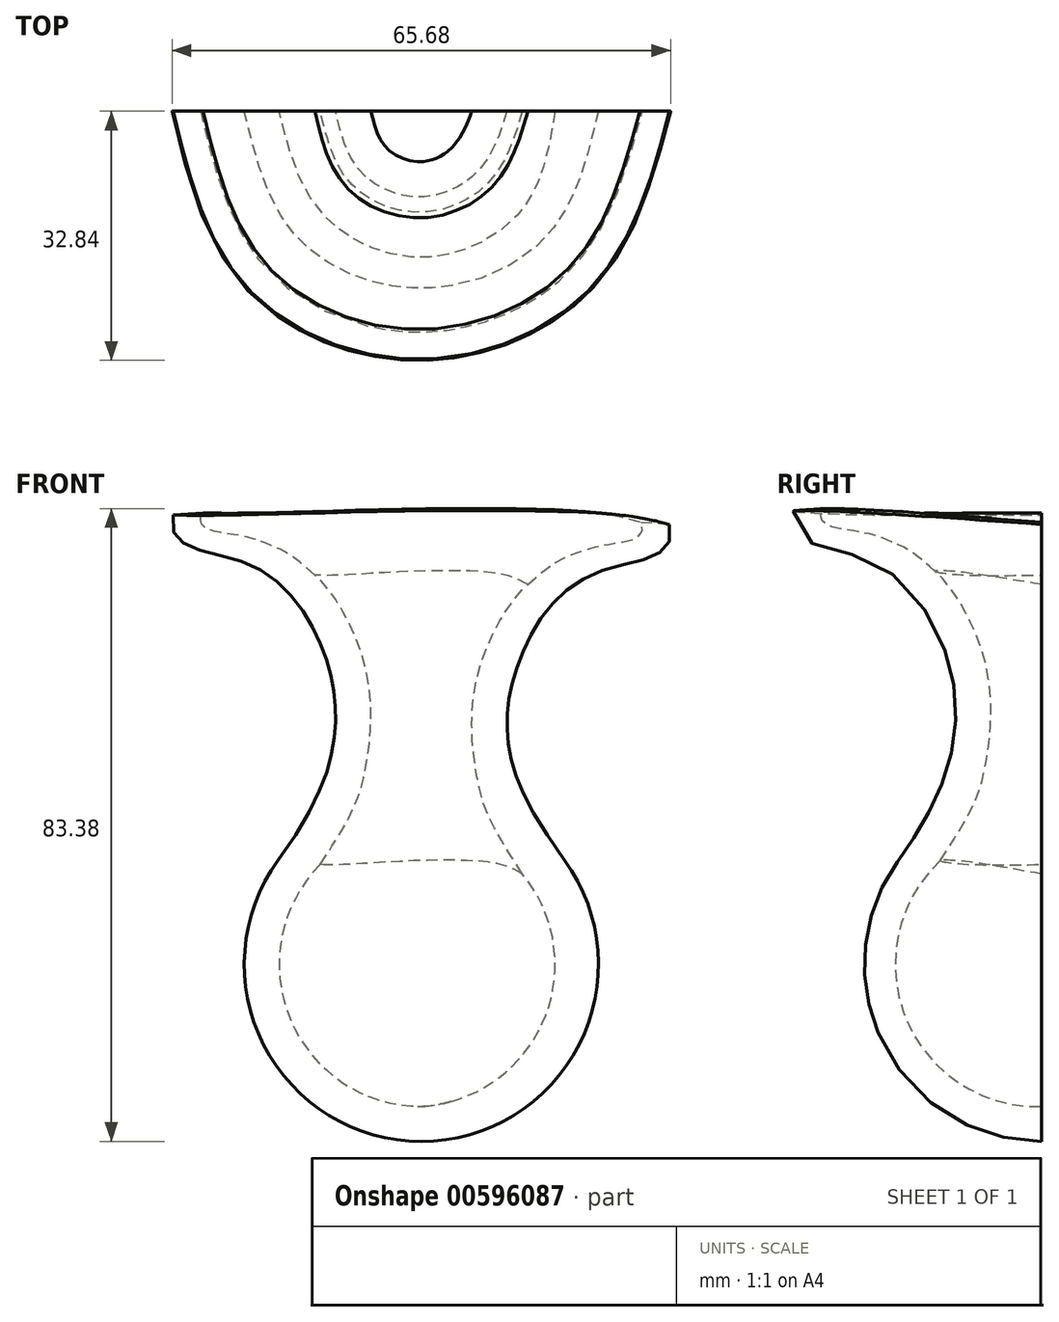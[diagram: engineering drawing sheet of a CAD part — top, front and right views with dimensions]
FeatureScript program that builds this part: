
annotation { "Feature Type Name" : "Feature", "Feature Type Description" : "" }
export const myFeature = defineFeature(function(context is Context, id is Id, definition is map)
    precondition{}
    {
        {
            var Q0;
            Q0=qCreatedBy(makeId("Front.planeOp"),FACE);
            var sketch = newSketch(context, id + "F0", { "sketchPlane" : qUnion([Q0])});
            skFitSpline(sketch, "E0", {"points": [v(-18.88, 13.69) * mm, v(-11.32, 31.6) * mm, v(-13.11, 41.8) * mm, v(-23.1, 52.87) * mm, v(-32.67, 59.2) * mm], "startDerivative": vector(59.38, 81.9) * mm, "endDerivative": vector(16.72, 63.85) * mm});
            skPoint(sketch, "E1.orphan", {"position": v(0, 59.2) * mm});
            skLineSegment(sketch, "E2.trimOffspring", {"start": v(0, -18.72) * mm, "end": v(0, -23.32) * mm});
            skFitSpline(sketch, "E3", {"points": [v(-13.32, 13.16) * mm, v(-7.45, 25.36) * mm, v(-7.45, 39.53) * mm, v(-14.04, 51.28) * mm], "startDerivative": vector(40, 60.94) * mm, "endDerivative": vector(-17.73, 13.1) * mm});
            skArc(sketch, "E4", {"start": v(-18.88, 13.69) * mm, "mid": v(-20.77, -10.6) * mm, "end": v(0, -23.32) * mm});
            skArc(sketch, "E5", {"start": v(-13.32, 13.16) * mm, "mid": v(-17.27, -7.22) * mm, "end": v(0, -18.72) * mm});
            skFitSpline(sketch, "E6", {"points": [v(-14.04, 51.28) * mm, v(-19.17, 54.93) * mm, v(-23.98, 56.49) * mm, v(-28.7, 57.72) * mm, v(-28.75, 59.48) * mm], "startDerivative": vector(-26.07, 24.13) * mm, "endDerivative": vector(8.86, 9.98) * mm});
            skLineSegment(sketch, "E7", {"start": v(-32.67, 59.2) * mm, "end": v(-28.75, 59.48) * mm});
            skSolve(sketch);
        }
        {
            var Q0;
            Q0=qCreatedBy(makeId("Front.planeOp"),FACE);
            var sketch = newSketch(context, id + "F1", { "sketchPlane" : qUnion([Q0])});
            skLineSegment(sketch, "E8", {"start": v(0, 0) * mm, "end": v(0, 58.67) * mm});
            skSolve(sketch);
        }
        {
            var Q0;
            Q0=sQuery(id+"F1.wireOp",EDGE,"E8");
            cPlane(context, id + "F2", {"entities" : qUnion([Q0]), "cplaneType" : CPlaneType.LINE_ANGLE, "offset" : 25.4 * mm, "angle" : 45 * degree, "width" : 152.4 * mm, "height" : 152.4 * mm});
        }
        {
            var Q0;
            Q0=qCreatedBy(id+"F2.planeOp",FACE);
            var sketch = newSketch(context, id + "F3", { "sketchPlane" : qUnion([Q0])});
            skFitSpline(sketch, "E9", {"points": [v(-18.88, 13.69) * mm, v(-10.9, 31.85) * mm, v(-12.7, 42.07) * mm, v(-22.69, 53.13) * mm, v(-32.25, 59.47) * mm], "startDerivative": vector(59.38, 81.9) * mm, "endDerivative": vector(16.72, 63.85) * mm});
            skLineSegment(sketch, "E10.trimOffspring", {"start": v(0, -18.72) * mm, "end": v(0, -23.32) * mm});
            skFitSpline(sketch, "E11", {"points": [v(-12.9, 13.42) * mm, v(-7.03, 25.62) * mm, v(-7.03, 39.8) * mm, v(-13.62, 51.55) * mm], "startDerivative": vector(40, 60.94) * mm, "endDerivative": vector(-17.73, 13.1) * mm});
            skArc(sketch, "E12", {"start": v(-18.88, 13.69) * mm, "mid": v(-20.77, -10.6) * mm, "end": v(0, -23.32) * mm});
            skArc(sketch, "E13", {"start": v(-12.9, 13.42) * mm, "mid": v(-17.22, -6.97) * mm, "end": v(0, -18.72) * mm});
            skFitSpline(sketch, "E14", {"points": [v(-13.62, 51.55) * mm, v(-18.74, 55.2) * mm, v(-23.55, 56.75) * mm, v(-28.27, 57.99) * mm, v(-28.33, 59.74) * mm], "startDerivative": vector(-26.07, 24.13) * mm, "endDerivative": vector(8.86, 9.98) * mm});
            skLineSegment(sketch, "E15", {"start": v(-32.25, 59.47) * mm, "end": v(-28.33, 59.74) * mm});
            skSolve(sketch);
        }
        {
            var Q0;
            Q0=sQuery(id+"F1.wireOp",EDGE,"E8");
            cPlane(context, id + "F4", {"entities" : qUnion([Q0]), "cplaneType" : CPlaneType.LINE_ANGLE, "offset" : 25.4 * mm, "angle" : 45 * degree, "oppositeDirection" : true, "width" : 152.4 * mm, "height" : 152.4 * mm});
        }
        {
            var Q0;
            Q0=qCreatedBy(id+"F4.planeOp",FACE);
            var sketch = newSketch(context, id + "F5", { "sketchPlane" : qUnion([Q0])});
            skFitSpline(sketch, "E16", {"points": [v(-18.88, 13.69) * mm, v(-11.32, 31.61) * mm, v(-13.11, 41.82) * mm, v(-23.1, 52.89) * mm, v(-32.67, 59.23) * mm], "startDerivative": vector(59.38, 81.9) * mm, "endDerivative": vector(16.72, 63.85) * mm});
            skLineSegment(sketch, "E17.trimOffspring", {"start": v(0, -18.72) * mm, "end": v(0, -23.32) * mm});
            skFitSpline(sketch, "E18", {"points": [v(-13.32, 13.17) * mm, v(-7.45, 25.38) * mm, v(-7.45, 39.55) * mm, v(-14.04, 51.3) * mm], "startDerivative": vector(40, 60.94) * mm, "endDerivative": vector(-17.73, 13.1) * mm});
            skArc(sketch, "E19", {"start": v(-18.88, 13.69) * mm, "mid": v(-20.77, -10.6) * mm, "end": v(0, -23.32) * mm});
            skArc(sketch, "E20", {"start": v(-13.32, 13.17) * mm, "mid": v(-17.3, -7.21) * mm, "end": v(0, -18.72) * mm});
            skFitSpline(sketch, "E21", {"points": [v(-14.04, 51.3) * mm, v(-19.17, 54.95) * mm, v(-23.98, 56.5) * mm, v(-28.7, 57.74) * mm, v(-28.75, 59.5) * mm], "startDerivative": vector(-26.07, 24.13) * mm, "endDerivative": vector(8.86, 9.98) * mm});
            skLineSegment(sketch, "E22", {"start": v(-32.67, 59.23) * mm, "end": v(-28.75, 59.5) * mm});
            skSolve(sketch);
        }
        {
            var Q0;
            Q0=sQuery(id+"F1.wireOp",EDGE,"E8");
            cPlane(context, id + "F6", {"entities" : qUnion([Q0]), "cplaneType" : CPlaneType.LINE_ANGLE, "offset" : 25.4 * mm, "angle" : 90 * degree, "width" : 152.4 * mm, "height" : 152.4 * mm});
        }
        {
            var Q0;
            Q0=qCreatedBy(id+"F6.planeOp",FACE);
            var sketch = newSketch(context, id + "F7", { "sketchPlane" : qUnion([Q0])});
            skFitSpline(sketch, "E23", {"points": [v(-18.88, 13.69) * mm, v(-11.32, 30.34) * mm, v(-13.11, 40.55) * mm, v(-23.1, 51.62) * mm, v(-32.67, 57.96) * mm], "startDerivative": vector(59.38, 81.9) * mm, "endDerivative": vector(16.72, 63.85) * mm});
            skLineSegment(sketch, "E24.trimOffspring", {"start": v(0, -18.72) * mm, "end": v(0, -23.32) * mm});
            skFitSpline(sketch, "E25", {"points": [v(-13.32, 11.9) * mm, v(-7.45, 24.1) * mm, v(-7.45, 38.28) * mm, v(-14.04, 50.03) * mm], "startDerivative": vector(40, 60.94) * mm, "endDerivative": vector(-17.73, 13.1) * mm});
            skArc(sketch, "E26", {"start": v(-18.88, 13.69) * mm, "mid": v(-20.77, -10.6) * mm, "end": v(0, -23.32) * mm});
            skArc(sketch, "E27", {"start": v(-13.32, 11.9) * mm, "mid": v(-16.06, -7.5) * mm, "end": v(0, -18.72) * mm});
            skFitSpline(sketch, "E28", {"points": [v(-14.04, 50.03) * mm, v(-19.17, 53.68) * mm, v(-23.98, 55.24) * mm, v(-28.7, 56.47) * mm, v(-28.75, 58.23) * mm], "startDerivative": vector(-26.07, 24.13) * mm, "endDerivative": vector(8.86, 9.98) * mm});
            skLineSegment(sketch, "E29", {"start": v(-32.67, 57.96) * mm, "end": v(-28.75, 58.23) * mm});
            skSolve(sketch);
        }
        {
            var Q0;
            Q0=sQuery(id+"F1.wireOp",EDGE,"E8");
            cPlane(context, id + "F8", {"entities" : qUnion([Q0]), "cplaneType" : CPlaneType.LINE_ANGLE, "offset" : 25.4 * mm, "angle" : 0 * degree, "width" : 152.4 * mm, "height" : 152.4 * mm});
        }
        {
            var Q0;
            Q0=qCreatedBy(id+"F8.planeOp",FACE);
            var sketch = newSketch(context, id + "F9", { "sketchPlane" : qUnion([Q0])});
            skFitSpline(sketch, "E30", {"points": [v(-18.88, 13.69) * mm, v(-11.32, 32.12) * mm, v(-13.11, 42.33) * mm, v(-23.1, 53.4) * mm, v(-32.67, 59.73) * mm], "startDerivative": vector(59.38, 81.9) * mm, "endDerivative": vector(16.72, 63.85) * mm});
            skLineSegment(sketch, "E31.trimOffspring", {"start": v(0, -18.72) * mm, "end": v(0, -23.32) * mm});
            skFitSpline(sketch, "E32", {"points": [v(-13.32, 13.68) * mm, v(-7.45, 25.89) * mm, v(-7.45, 40.06) * mm, v(-14.04, 51.81) * mm], "startDerivative": vector(40, 60.94) * mm, "endDerivative": vector(-17.73, 13.1) * mm});
            skArc(sketch, "E33", {"start": v(-18.88, 13.69) * mm, "mid": v(-20.77, -10.6) * mm, "end": v(0, -23.32) * mm});
            skArc(sketch, "E34", {"start": v(-13.32, 13.68) * mm, "mid": v(-17.86, -7.12) * mm, "end": v(0, -18.72) * mm});
            skFitSpline(sketch, "E35", {"points": [v(-14.04, 51.81) * mm, v(-19.17, 55.46) * mm, v(-23.98, 57.01) * mm, v(-28.7, 58.25) * mm, v(-28.75, 60) * mm], "startDerivative": vector(-26.07, 24.13) * mm, "endDerivative": vector(8.86, 9.98) * mm});
            skLineSegment(sketch, "E36", {"start": v(-32.67, 59.73) * mm, "end": v(-28.75, 60) * mm});
            skSolve(sketch);
        }
        {
            var Q0;
            Q0=makeQuery(id+"F7.imprint","IMPRINT",FACE,{"disambiguationData":[TD([[makeQuery(id+"F7.imprint","IMPRINT",EDGE,{"derivedFrom":sQuery(id+"F7.wireOp",EDGE,"E23")}),-1.0]])]});
            var Q1;
            Q1=makeQuery(id+"F3.imprint","IMPRINT",FACE,{"disambiguationData":[TD([[makeQuery(id+"F3.imprint","IMPRINT",EDGE,{"derivedFrom":sQuery(id+"F3.wireOp",EDGE,"E9")}),-1.0]])]});
            var Q2;
            Q2=makeQuery(id+"F9.imprint","IMPRINT",FACE,{"disambiguationData":[TD([[makeQuery(id+"F9.imprint","IMPRINT",EDGE,{"derivedFrom":sQuery(id+"F9.wireOp",EDGE,"E30")}),-1.0]])]});
            var Q3;
            Q3=makeQuery(id+"F5.imprint","IMPRINT",FACE,{"disambiguationData":[TD([[makeQuery(id+"F5.imprint","IMPRINT",EDGE,{"derivedFrom":sQuery(id+"F5.wireOp",EDGE,"E16")}),-1.0]])]});
            var Q4;
            Q4=makeQuery(id+"F0.imprint","IMPRINT",FACE,{"disambiguationData":[TD([[makeQuery(id+"F0.imprint","IMPRINT",EDGE,{"derivedFrom":sQuery(id+"F0.wireOp",EDGE,"E0")}),-1.0]])]});
            loft(context, id + "F10", {"sheetProfilesArray" : [{ "sheetProfileEntities" : qUnion([Q0]) }, { "sheetProfileEntities" : qUnion([Q1]) }, { "sheetProfileEntities" : qUnion([Q2]) }, { "sheetProfileEntities" : qUnion([Q3]) }, { "sheetProfileEntities" : qUnion([Q4]) }]});
        }
    });
